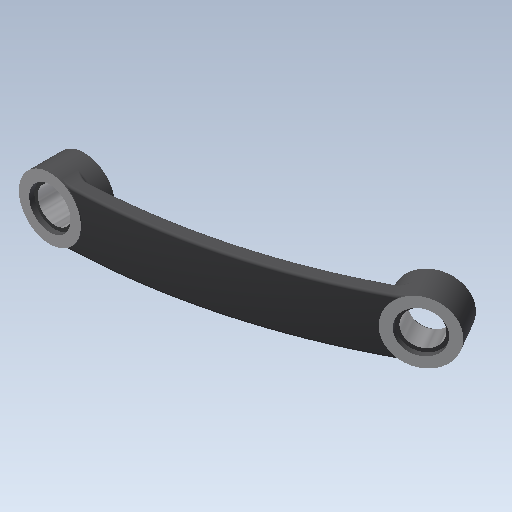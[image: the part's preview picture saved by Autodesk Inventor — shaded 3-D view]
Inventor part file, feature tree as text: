
AUTODESK INVENTOR PART (.ipt)
format: ipt  version: 2020.1 (Build 241239000, 239)  size: 294,400 bytes
history: native  units: mm
features: hole x6, sketch x5, plane x3, extrude x3, fillet x3, other x2, thicken_offset x1, revolve x1
ambient origin geometry x8: Origin, YZ Plane, XZ Plane, XY Plane, X Axis, Y Axis, Z Axis, Center Point
bodies: Solid1 (feature_tree)
feature tree (24):
  sketch  "3D Sketch1"
  plane  "Work Plane1"
  sketch  "Sketch2"  dims[d2=170.0mm d4=170.0mm]
  thicken_offset  "Thicken1"
  extrude  "Extrusion1"  TaperAngle=180.0deg  [1 undecoded]
  plane  "Work Plane2"
  extrude  "Extrusion2"  Depth=170.0mm
  plane  "Work Plane3"
  extrude  "Extrusion3"  Depth=4.0mm
  hole  "Hole1"  [1 undecoded]
  hole  "Hole2"  [1 undecoded]
  fillet  "Fillet1"  Radius=18.0mm
  fillet  "Fillet2"  Radius=10.0mm
  fillet  "Fillet3"  Radius=10.0mm
  hole  "Hole4"  [1 undecoded]
  hole  "Hole5"  [1 undecoded]
  hole  "Hole6"  [1 undecoded]
  hole  "Hole7"  [1 undecoded]
  sketch  "Sketch1"  dims[d0=170.0mm d1=180.0deg]
  other  "Srf1"
  sketch  "Sketch3"  dims[d5=16.0mm d6=4.0mm d7=8.0mm]
  sketch  "Sketch4"  dims[d8=10.0mm d9=0.0mm d10=18.0mm d11=10.0mm d12=0.0mm d13=18.0mm d14=10.0mm d15=0.0mm d16=10.0mm d17=10.0mm d18=10.0mm d19=6.0mm d20=4.0mm d21=2.0mm d22=90.0deg d23=8.0mm d24=20.594885mm d25=10.0mm d26=10.0mm d27=10.0mm d28=6.0mm d29=4.0mm d30=2.0mm d31=90.0deg d32=8.0mm d33=20.594885mm d34=1.0mm d35=10.0mm d36=0.7mm d52=30.0deg d53=10.0mm d54=10.0mm d55=12.0mm d56=6.0mm d57=4.0mm d58=2.0mm d59=90.0deg d60=1.5mm d61=0.0mm d62=10.0mm d63=10.0mm d64=12.0mm d65=6.0mm d66=4.0mm d67=2.0mm d68=90.0deg d69=1.5mm d70=0.0mm d71=10.0mm d72=10.0mm d73=12.0mm d74=6.0mm d75=4.0mm d76=2.0mm d77=90.0deg d78=1.5mm d79=0.0mm d80=10.0mm d81=10.0mm d82=12.0mm d83=6.0mm d84=4.0mm d85=2.0mm d86=90.0deg d87=1.5mm d88=0.0mm]
  revolve  "RevolutionSrf1"  Angle=30.0deg
  other  "3D Intersection1"
note: 7 required parameter values undecoded (feature->parameter linkage not recoverable at this tier; creation-order binding heuristic only, values carry confidence <= 0.55)
